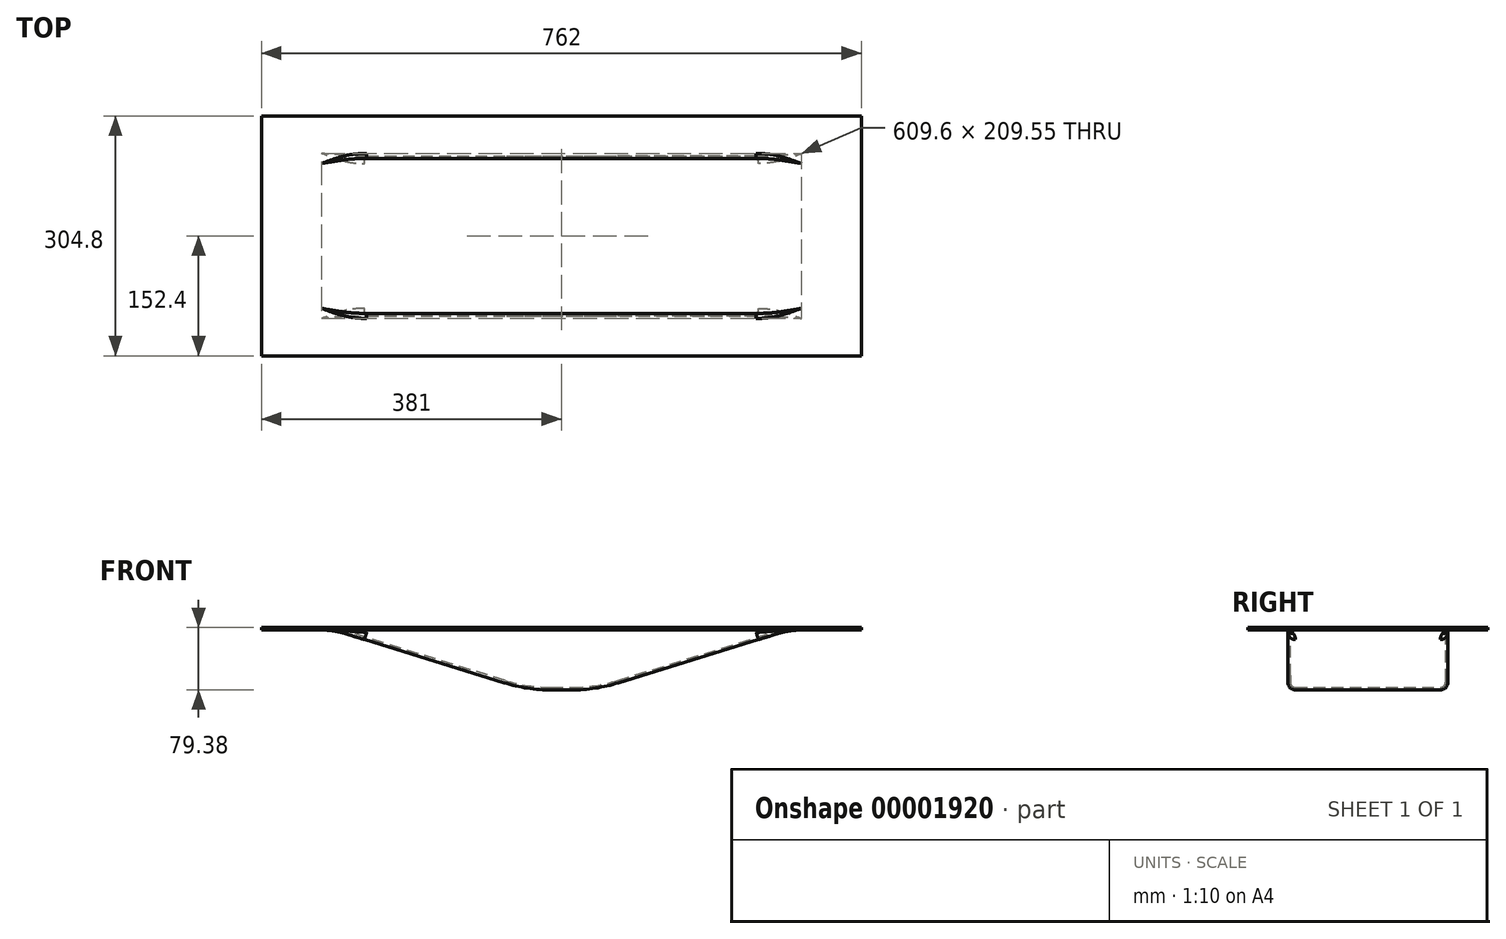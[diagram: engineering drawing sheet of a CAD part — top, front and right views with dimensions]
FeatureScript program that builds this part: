
annotation { "Feature Type Name" : "Feature", "Feature Type Description" : "" }
export const myFeature = defineFeature(function(context is Context, id is Id, definition is map)
    precondition{}
    {
        {
            var Q0;
            Q0=qCreatedBy(makeId("Top.planeOp"),FACE);
            var sketch = newSketch(context, id + "F0", { "sketchPlane" : qUnion([Q0])});
            skLineSegment(sketch, "E0.bottom", {"start": v(-381, 152.4) * mm, "end": v(381, 152.4) * mm});
            skLineSegment(sketch, "E0.top", {"start": v(-381, -152.4) * mm, "end": v(381, -152.4) * mm});
            skLineSegment(sketch, "E0.left", {"start": v(-381, 152.4) * mm, "end": v(-381, -152.4) * mm});
            skLineSegment(sketch, "E0.right", {"start": v(381, 152.4) * mm, "end": v(381, -152.4) * mm});
            skLineSegment(sketch, "E1.bottom", {"start": v(-304.8, 101.6) * mm, "end": v(304.8, 101.6) * mm});
            skLineSegment(sketch, "E1.top", {"start": v(-304.8, -101.6) * mm, "end": v(304.8, -101.6) * mm});
            skLineSegment(sketch, "E1.left", {"start": v(-304.8, 101.6) * mm, "end": v(-304.8, -101.6) * mm});
            skLineSegment(sketch, "E1.right", {"start": v(304.8, 101.6) * mm, "end": v(304.8, -101.6) * mm});
            skLineSegment(sketch, "E2", {"start": v(0, 152.4) * mm, "end": v(0, 101.6) * mm, "construction": true});
            skLineSegment(sketch, "E3", {"start": v(0, 101.6) * mm, "end": v(0, 0) * mm, "construction": true});
            skLineSegment(sketch, "E4", {"start": v(0, 0) * mm, "end": v(304.8, 0) * mm, "construction": true});
            skLineSegment(sketch, "E5", {"start": v(304.8, 0) * mm, "end": v(381, 0) * mm, "construction": true});
            skSolve(sketch);
        }
        {
            var Q0;
            Q0=makeQuery(id+"F0.imprint","IMPRINT",FACE,{"disambiguationData":[TD([[makeQuery(id+"F0.imprint","IMPRINT",EDGE,{"derivedFrom":sQuery(id+"F0.wireOp",EDGE,"E0.bottom")}),-1.0]])]});
            extrude(context, id + "F1", {"entities" : qUnion([Q0]), "oppositeDirection" : true, "depth" : 3.17 * mm});
        }
        {
            var Q0;
            Q0=qCreatedBy(makeId("Front.planeOp"),FACE);
            var sketch = newSketch(context, id + "F2", { "sketchPlane" : qUnion([Q0])});
            skArc(sketch, "E6", {"start": v(-274.8, -4.53) * mm, "mid": v(-289.63, -1.14) * mm, "end": v(-304.8, 0) * mm});
            skLineSegment(sketch, "E7", {"start": v(-274.8, -4.53) * mm, "end": v(-71.76, -67.28) * mm});
            skArc(sketch, "E8", {"start": v(-71.76, -67.28) * mm, "mid": v(-42.57, -73.96) * mm, "end": v(-12.7, -76.2) * mm});
            skLineSegment(sketch, "E9", {"start": v(-12.7, -76.2) * mm, "end": v(0, -76.2) * mm});
            skLineSegment(sketch, "E10", {"start": v(0, -76.2) * mm, "end": v(0, 0) * mm, "construction": true});
            skLineSegment(sketch, "E11.0.MirrorCS", {"start": v(12.7, -76.2) * mm, "end": v(0, -76.2) * mm});
            skArc(sketch, "E12.0.MirrorCS", {"start": v(71.76, -67.28) * mm, "mid": v(42.57, -73.96) * mm, "end": v(12.7, -76.2) * mm});
            skLineSegment(sketch, "E13.0.MirrorCS", {"start": v(274.8, -4.53) * mm, "end": v(71.76, -67.28) * mm});
            skArc(sketch, "E14.0.MirrorCS", {"start": v(274.8, -4.53) * mm, "mid": v(289.63, -1.14) * mm, "end": v(304.8, 0) * mm});
            skLineSegment(sketch, "E15", {"start": v(-275.74, -7.56) * mm, "end": v(-72.7, -70.31) * mm});
            skArc(sketch, "E16", {"start": v(-72.7, -70.31) * mm, "mid": v(-43.04, -77.1) * mm, "end": v(-12.7, -79.38) * mm});
            skLineSegment(sketch, "E17", {"start": v(-12.7, -79.38) * mm, "end": v(0, -79.38) * mm});
            skLineSegment(sketch, "E18.0.MirrorCS", {"start": v(12.7, -79.38) * mm, "end": v(0, -79.38) * mm});
            skArc(sketch, "E19.0.MirrorCS", {"start": v(72.7, -70.31) * mm, "mid": v(43.04, -77.1) * mm, "end": v(12.7, -79.38) * mm});
            skLineSegment(sketch, "E20.0.MirrorCS", {"start": v(275.74, -7.56) * mm, "end": v(72.7, -70.31) * mm});
            skArc(sketch, "E21.0.MirrorCS", {"start": v(275.74, -7.56) * mm, "mid": v(290.1, -4.28) * mm, "end": v(304.8, -3.17) * mm});
            skLineSegment(sketch, "E22", {"start": v(-304.8, 0) * mm, "end": v(-304.8, -3.18) * mm});
            skLineSegment(sketch, "E23.0.MirrorCS", {"start": v(304.8, 0) * mm, "end": v(304.8, -3.18) * mm});
            skArc(sketch, "E24", {"start": v(-275.74, -7.56) * mm, "mid": v(-290.1, -4.28) * mm, "end": v(-304.8, -3.17) * mm});
            skSolve(sketch);
        }
        {
            var Q0;
            Q0 = qSketchRegion(id + "F2", true);
            var Q1;
            Q1=makeQuery(id+"F1.opExtrude","SWEPT_FACE",FACE,{"disambiguationData":[OSD([sQuery(id+"F0.wireOp",EDGE,"E1.top")])]});
            extrude(context, id + "F3", {"entities" : qUnion([Q0]), "operationType" : NewBodyOperationType.ADD, "endBound" : BoundingType.SYMMETRIC, "endBoundEntity" : qUnion([Q1]), "depth" : 203.2 * mm});
        }
        {
            var Q0;
            Q0=makeQuery(id+"F1.opExtrude","SWEPT_FACE",FACE,{"disambiguationData":[OSD([sQuery(id+"F0.wireOp",EDGE,"E1.bottom")])]});
            var sketch = newSketch(context, id + "F4", { "sketchPlane" : qUnion([Q0])});
            skLineSegment(sketch, "E25.0", {"start": v(-304.8, 0) * mm, "end": v(304.8, 0) * mm});
            skLineSegment(sketch, "E26.0", {"start": v(-304.8, 0) * mm, "end": v(-304.8, -3.18) * mm});
            skLineSegment(sketch, "E26.2", {"start": v(-275.74, -7.56) * mm, "end": v(-72.7, -70.31) * mm});
            skArc(sketch, "E26.3", {"start": v(-72.7, -70.31) * mm, "mid": v(-43.04, -77.1) * mm, "end": v(-12.7, -79.38) * mm});
            skLineSegment(sketch, "E26.4", {"start": v(-12.7, -79.38) * mm, "end": v(0, -79.38) * mm});
            skLineSegment(sketch, "E26.5", {"start": v(12.7, -79.38) * mm, "end": v(0, -79.38) * mm});
            skArc(sketch, "E26.6", {"start": v(72.7, -70.31) * mm, "mid": v(43.04, -77.1) * mm, "end": v(12.7, -79.38) * mm});
            skLineSegment(sketch, "E26.7", {"start": v(275.74, -7.56) * mm, "end": v(72.7, -70.31) * mm});
            skArc(sketch, "E26.8", {"start": v(275.74, -7.56) * mm, "mid": v(290.1, -4.28) * mm, "end": v(304.8, -3.17) * mm});
            skLineSegment(sketch, "E26.9", {"start": v(304.8, 0) * mm, "end": v(304.8, -3.18) * mm});
            skArc(sketch, "E27.0", {"start": v(-275.74, -7.56) * mm, "mid": v(-290.1, -4.28) * mm, "end": v(-304.8, -3.17) * mm});
            skSolve(sketch);
        }
        {
            var Q0;
            Q0 = qSketchRegion(id + "F4", true);
            extrude(context, id + "F5", {"entities" : qUnion([Q0]), "depth" : 3.17 * mm});
        }
        {
            var Q0;
            Q0=makeQuery(id+"F5.opExtrude","SWEPT_BODY",BODY,{"disambiguationData":[OSD([sQuery(id+"F4.wireOp",EDGE,"E25.0"),sQuery(id+"F4.wireOp",EDGE,"E26.0"),sQuery(id+"F4.wireOp",EDGE,"E26.2"),sQuery(id+"F4.wireOp",EDGE,"E26.3"),sQuery(id+"F4.wireOp",EDGE,"E26.4"),sQuery(id+"F4.wireOp",EDGE,"E26.6"),sQuery(id+"F4.wireOp",EDGE,"E26.7"),sQuery(id+"F4.wireOp",EDGE,"E26.8"),sQuery(id+"F4.wireOp",EDGE,"E26.9"),sQuery(id+"F4.wireOp",EDGE,"E27.0")])]});
            var Q1;
            Q1=qCreatedBy(makeId("Front.planeOp"),FACE);
            mirror(context, id + "F6", {"entities" : qUnion([Q0]), "mirrorPlane" : qUnion([Q1])});
        }
        {
            var Q0;
            Q0=makeQuery(id+"F1.opExtrude","SWEPT_BODY",BODY,{"disambiguationData":[OSD([sQuery(id+"F0.wireOp",EDGE,"E0.bottom"),sQuery(id+"F0.wireOp",EDGE,"E0.top"),sQuery(id+"F0.wireOp",EDGE,"E0.left"),sQuery(id+"F0.wireOp",EDGE,"E0.right"),sQuery(id+"F0.wireOp",EDGE,"E1.bottom"),sQuery(id+"F0.wireOp",EDGE,"E1.top"),sQuery(id+"F0.wireOp",EDGE,"E1.left"),sQuery(id+"F0.wireOp",EDGE,"E1.right")])]});
            var Q1;
            Q1=makeQuery(id+"F5.opExtrude","SWEPT_BODY",BODY,{"disambiguationData":[OSD([sQuery(id+"F4.wireOp",EDGE,"E25.0"),sQuery(id+"F4.wireOp",EDGE,"E26.0"),sQuery(id+"F4.wireOp",EDGE,"E26.2"),sQuery(id+"F4.wireOp",EDGE,"E26.3"),sQuery(id+"F4.wireOp",EDGE,"E26.4"),sQuery(id+"F4.wireOp",EDGE,"E26.6"),sQuery(id+"F4.wireOp",EDGE,"E26.7"),sQuery(id+"F4.wireOp",EDGE,"E26.8"),sQuery(id+"F4.wireOp",EDGE,"E26.9"),sQuery(id+"F4.wireOp",EDGE,"E27.0")])]});
            var Q2;
            Q2=makeQuery(id+"F6.opPattern","COPY",BODY,{"derivedFrom":makeQuery(id+"F5.opExtrude","SWEPT_BODY",BODY,{"disambiguationData":[OSD([sQuery(id+"F4.wireOp",EDGE,"E25.0"),sQuery(id+"F4.wireOp",EDGE,"E26.0"),sQuery(id+"F4.wireOp",EDGE,"E26.2"),sQuery(id+"F4.wireOp",EDGE,"E26.3"),sQuery(id+"F4.wireOp",EDGE,"E26.4"),sQuery(id+"F4.wireOp",EDGE,"E26.6"),sQuery(id+"F4.wireOp",EDGE,"E26.7"),sQuery(id+"F4.wireOp",EDGE,"E26.8"),sQuery(id+"F4.wireOp",EDGE,"E26.9"),sQuery(id+"F4.wireOp",EDGE,"E27.0")])]}),"instanceName":"1"});
            booleanBodies(context, id + "F7", {"operationType" : BooleanOperationType.UNION, "tools" : qUnion([Q0, Q1, Q2])});
        }
        {
            var Q0;
            Q0=makeQuery(id+"F7.opBoolean","INTERSECT",EDGE,{"derivedFrom":[makeQuery(id+"F3.opExtrude","SWEPT_FACE",FACE,{"disambiguationData":[OSD([sQuery(id+"F2.wireOp",EDGE,"E7")])]}),makeQuery(id+"F5.opExtrude","CAP_FACE",FACE,{"disambiguationData":[OSD([sQuery(id+"F4.wireOp",EDGE,"E25.0"),sQuery(id+"F4.wireOp",EDGE,"E26.0"),sQuery(id+"F4.wireOp",EDGE,"E26.2"),sQuery(id+"F4.wireOp",EDGE,"E26.3"),sQuery(id+"F4.wireOp",EDGE,"E26.4"),sQuery(id+"F4.wireOp",EDGE,"E26.6"),sQuery(id+"F4.wireOp",EDGE,"E26.7"),sQuery(id+"F4.wireOp",EDGE,"E26.8"),sQuery(id+"F4.wireOp",EDGE,"E26.9"),sQuery(id+"F4.wireOp",EDGE,"E27.0")])],"isStart":false})]});
            var Q1;
            Q1=makeQuery(id+"F7.opBoolean","INTERSECT",EDGE,{"derivedFrom":[makeQuery(id+"F3.opExtrude","SWEPT_FACE",FACE,{"disambiguationData":[OSD([sQuery(id+"F2.wireOp",EDGE,"E7")])]}),makeQuery(id+"F6.opPattern","COPY",FACE,{"derivedFrom":makeQuery(id+"F5.opExtrude","CAP_FACE",FACE,{"disambiguationData":[OSD([sQuery(id+"F4.wireOp",EDGE,"E25.0"),sQuery(id+"F4.wireOp",EDGE,"E26.0"),sQuery(id+"F4.wireOp",EDGE,"E26.2"),sQuery(id+"F4.wireOp",EDGE,"E26.3"),sQuery(id+"F4.wireOp",EDGE,"E26.4"),sQuery(id+"F4.wireOp",EDGE,"E26.6"),sQuery(id+"F4.wireOp",EDGE,"E26.7"),sQuery(id+"F4.wireOp",EDGE,"E26.8"),sQuery(id+"F4.wireOp",EDGE,"E26.9"),sQuery(id+"F4.wireOp",EDGE,"E27.0")])],"isStart":false}),"instanceName":"1"})]});
            var Q2;
            Q2=makeQuery(id+"F5.opExtrude","CAP_EDGE",EDGE,{"disambiguationData":[OSD([sQuery(id+"F4.wireOp",EDGE,"E25.0")])],"isStart":false});
            var Q3;
            Q3=makeQuery(id+"F6.opPattern","COPY",EDGE,{"derivedFrom":makeQuery(id+"F5.opExtrude","CAP_EDGE",EDGE,{"disambiguationData":[OSD([sQuery(id+"F4.wireOp",EDGE,"E25.0")])],"isStart":false}),"instanceName":"1"});
            fillet(context, id + "F8", {"entities" : qUnion([Q0, Q1, Q2, Q3]), "radius" : 6.35 * mm, "tangentPropagation" : true, "allowEdgeOverflow" : false});
        }
        {
            var Q0;
            {var subQ0=sQuery(id+"F0.wireOp",EDGE,"E1.top");var subQ1=makeQuery(id+"F1.opExtrude","CAP_EDGE",EDGE,{"disambiguationData":[OSD([subQ0])],"isStart":false});var subQ2=sQuery(id+"F2.wireOp",EDGE,"E24");var subQ3=sQuery(id+"F2.wireOp",EDGE,"E6");var subQ4=sQuery(id+"F2.wireOp",EDGE,"E14.0.MirrorCS");var subQ5=sQuery(id+"F2.wireOp",EDGE,"E21.0.MirrorCS");var subQ6=makeQuery(id+"F3.opExtrude","CAP_FACE",FACE,{"disambiguationData":[OSD([subQ3,sQuery(id+"F2.wireOp",EDGE,"E7"),sQuery(id+"F2.wireOp",EDGE,"E8"),sQuery(id+"F2.wireOp",EDGE,"E11.0.MirrorCS"),sQuery(id+"F2.wireOp",EDGE,"E12.0.MirrorCS"),sQuery(id+"F2.wireOp",EDGE,"E13.0.MirrorCS"),subQ4,sQuery(id+"F2.wireOp",EDGE,"E15"),sQuery(id+"F2.wireOp",EDGE,"E16"),sQuery(id+"F2.wireOp",EDGE,"E17"),sQuery(id+"F2.wireOp",EDGE,"E19.0.MirrorCS"),sQuery(id+"F2.wireOp",EDGE,"E20.0.MirrorCS"),subQ5,sQuery(id+"F2.wireOp",EDGE,"E22"),sQuery(id+"F2.wireOp",EDGE,"E23.0.MirrorCS"),subQ2])],"isStart":false});var subQ7=makeQuery(id+"F3.opExtrude","SWEPT_FACE",FACE,{"disambiguationData":[OSD([subQ3])]});var subQ8=makeQuery(id+"F1.opExtrude","SWEPT_FACE",FACE,{"disambiguationData":[OSD([subQ0])]});var subQ9=makeQuery(id+"F1.opExtrude","CAP_FACE",FACE,{"disambiguationData":[OSD([sQuery(id+"F0.wireOp",EDGE,"E0.bottom"),sQuery(id+"F0.wireOp",EDGE,"E0.top"),sQuery(id+"F0.wireOp",EDGE,"E0.left"),sQuery(id+"F0.wireOp",EDGE,"E0.right"),sQuery(id+"F0.wireOp",EDGE,"E1.bottom"),subQ0,sQuery(id+"F0.wireOp",EDGE,"E1.left"),sQuery(id+"F0.wireOp",EDGE,"E1.right")])],"isStart":false});var subQ10=makeQuery(id+"F3.opExtrude","SWEPT_FACE",FACE,{"disambiguationData":[OSD([subQ4])]});Q0=makeQuery(id+"F7.opBoolean","MERGE",EDGE,{"derivedFrom":[makeQuery(id+"F3.boolean.opBoolean","SPLIT",EDGE,{"disambiguationData":[TD([subQ9,subQ8,subQ7,subQ6,makeQuery(id+"F3.opExtrude","SWEPT_FACE",FACE,{"disambiguationData":[OSD([subQ2])]})])],"derivedFrom":subQ1}),makeQuery(id+"F3.boolean.opBoolean","SPLIT",EDGE,{"disambiguationData":[TD([subQ9,subQ8,subQ6,subQ10,makeQuery(id+"F3.opExtrude","SWEPT_FACE",FACE,{"disambiguationData":[OSD([subQ5])]})])],"derivedFrom":subQ1}),makeQuery(id+"F3.boolean.opBoolean","SPLIT",EDGE,{"disambiguationData":[TD([subQ9,subQ8,subQ7,subQ6,subQ10])],"derivedFrom":subQ1})]});}
            var Q1;
            {var subQ0=sQuery(id+"F0.wireOp",EDGE,"E1.bottom");var subQ1=makeQuery(id+"F1.opExtrude","CAP_EDGE",EDGE,{"disambiguationData":[OSD([subQ0])],"isStart":false});var subQ2=sQuery(id+"F2.wireOp",EDGE,"E24");var subQ3=sQuery(id+"F2.wireOp",EDGE,"E6");var subQ4=sQuery(id+"F2.wireOp",EDGE,"E14.0.MirrorCS");var subQ5=sQuery(id+"F2.wireOp",EDGE,"E21.0.MirrorCS");var subQ6=makeQuery(id+"F3.opExtrude","CAP_FACE",FACE,{"disambiguationData":[OSD([subQ3,sQuery(id+"F2.wireOp",EDGE,"E7"),sQuery(id+"F2.wireOp",EDGE,"E8"),sQuery(id+"F2.wireOp",EDGE,"E11.0.MirrorCS"),sQuery(id+"F2.wireOp",EDGE,"E12.0.MirrorCS"),sQuery(id+"F2.wireOp",EDGE,"E13.0.MirrorCS"),subQ4,sQuery(id+"F2.wireOp",EDGE,"E15"),sQuery(id+"F2.wireOp",EDGE,"E16"),sQuery(id+"F2.wireOp",EDGE,"E17"),sQuery(id+"F2.wireOp",EDGE,"E19.0.MirrorCS"),sQuery(id+"F2.wireOp",EDGE,"E20.0.MirrorCS"),subQ5,sQuery(id+"F2.wireOp",EDGE,"E22"),sQuery(id+"F2.wireOp",EDGE,"E23.0.MirrorCS"),subQ2])],"isStart":true});var subQ7=makeQuery(id+"F3.opExtrude","SWEPT_FACE",FACE,{"disambiguationData":[OSD([subQ3])]});var subQ8=makeQuery(id+"F1.opExtrude","SWEPT_FACE",FACE,{"disambiguationData":[OSD([subQ0])]});var subQ9=makeQuery(id+"F1.opExtrude","CAP_FACE",FACE,{"disambiguationData":[OSD([sQuery(id+"F0.wireOp",EDGE,"E0.bottom"),sQuery(id+"F0.wireOp",EDGE,"E0.top"),sQuery(id+"F0.wireOp",EDGE,"E0.left"),sQuery(id+"F0.wireOp",EDGE,"E0.right"),subQ0,sQuery(id+"F0.wireOp",EDGE,"E1.top"),sQuery(id+"F0.wireOp",EDGE,"E1.left"),sQuery(id+"F0.wireOp",EDGE,"E1.right")])],"isStart":false});var subQ10=makeQuery(id+"F3.opExtrude","SWEPT_FACE",FACE,{"disambiguationData":[OSD([subQ4])]});Q1=makeQuery(id+"F7.opBoolean","MERGE",EDGE,{"derivedFrom":[makeQuery(id+"F3.boolean.opBoolean","SPLIT",EDGE,{"disambiguationData":[TD([subQ9,subQ8,subQ7,subQ6,makeQuery(id+"F3.opExtrude","SWEPT_FACE",FACE,{"disambiguationData":[OSD([subQ2])]})])],"derivedFrom":subQ1}),makeQuery(id+"F3.boolean.opBoolean","SPLIT",EDGE,{"disambiguationData":[TD([subQ9,subQ8,subQ6,subQ10,makeQuery(id+"F3.opExtrude","SWEPT_FACE",FACE,{"disambiguationData":[OSD([subQ5])]})])],"derivedFrom":subQ1}),makeQuery(id+"F3.boolean.opBoolean","SPLIT",EDGE,{"disambiguationData":[TD([subQ9,subQ8,subQ7,subQ6,subQ10])],"derivedFrom":subQ1})]});}
            fillet(context, id + "F9", {"entities" : qUnion([Q0, Q1]), "radius" : 3.17 * mm, "tangentPropagation" : true, "allowEdgeOverflow" : false});
        }
        {
            var Q0;
            Q0=makeQuery(id+"F3.opExtrude","CAP_EDGE",EDGE,{"disambiguationData":[OSD([sQuery(id+"F2.wireOp",EDGE,"E20.0.MirrorCS")])],"isStart":true});
            var Q1;
            Q1=makeQuery(id+"F3.opExtrude","CAP_EDGE",EDGE,{"disambiguationData":[OSD([sQuery(id+"F2.wireOp",EDGE,"E20.0.MirrorCS")])],"isStart":false});
            fillet(context, id + "F10", {"entities" : qUnion([Q0, Q1]), "radius" : 9.52 * mm, "tangentPropagation" : true, "allowEdgeOverflow" : false});
        }
    });
